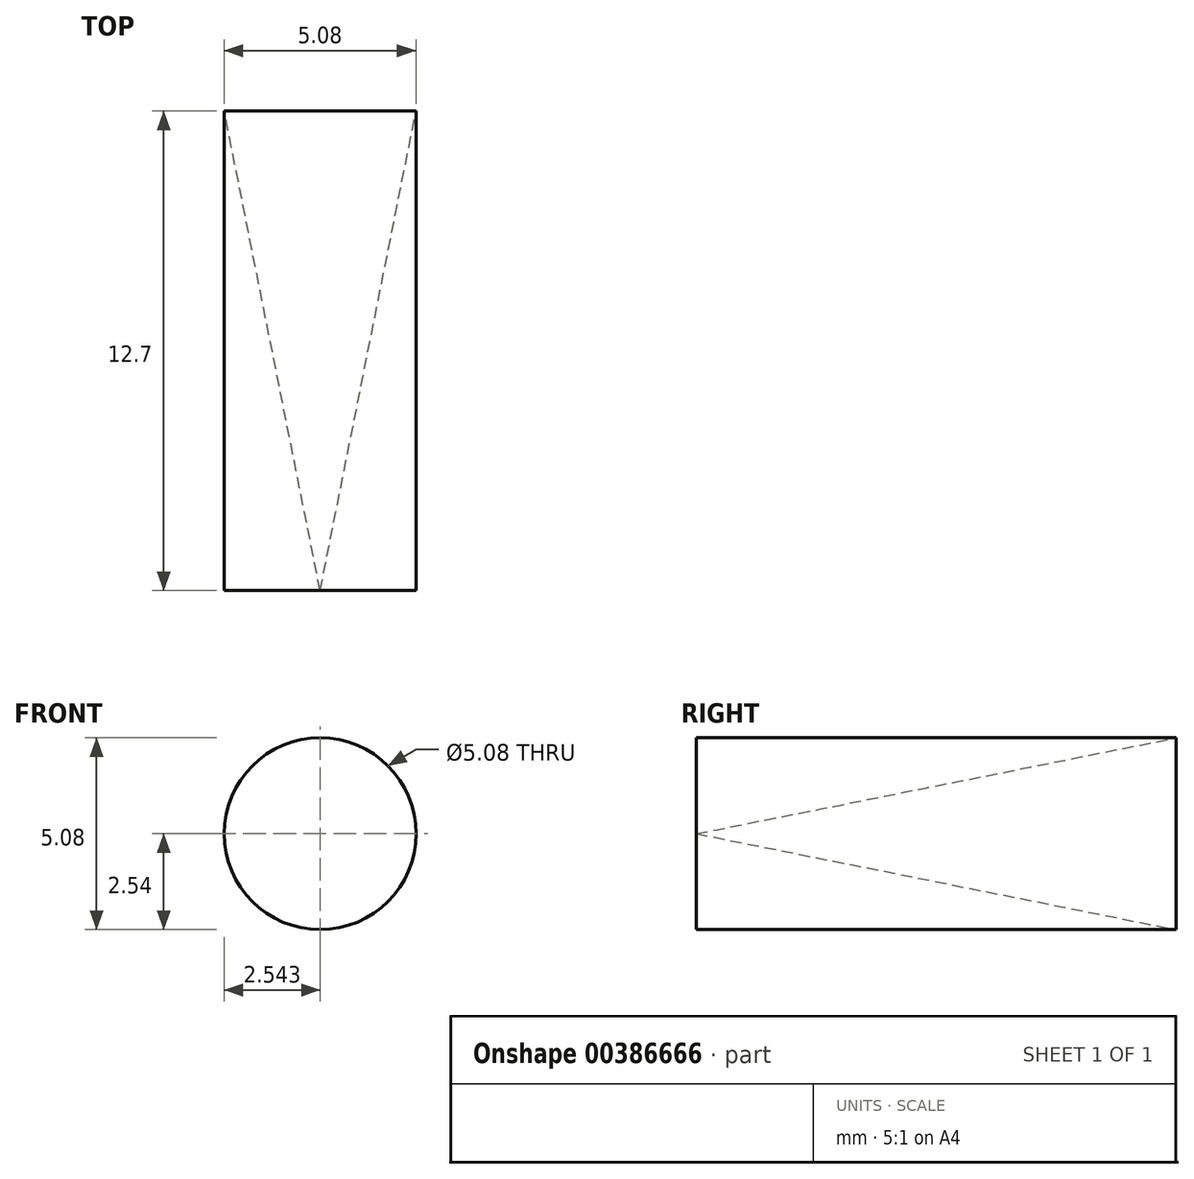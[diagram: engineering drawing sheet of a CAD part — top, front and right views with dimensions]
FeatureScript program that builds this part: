
annotation { "Feature Type Name" : "Feature", "Feature Type Description" : "" }
export const myFeature = defineFeature(function(context is Context, id is Id, definition is map)
    precondition{}
    {
        {
            var Q0;
            Q0=qCreatedBy(makeId("Top.planeOp"),FACE);
            var sketch = newSketch(context, id + "F0", { "sketchPlane" : qUnion([Q0])});
            skLineSegment(sketch, "E0", {"start": v(-59.2, 28.21) * mm, "end": v(-59.2, 15.51) * mm});
            skLineSegment(sketch, "E1", {"start": v(-59.2, 15.51) * mm, "end": v(-56.67, 15.51) * mm});
            skLineSegment(sketch, "E2", {"start": v(-56.67, 15.51) * mm, "end": v(-59.2, 28.21) * mm});
            skLineSegment(sketch, "E3", {"start": v(-56.67, 28.21) * mm, "end": v(-56.67, 15.51) * mm, "construction": true});
            skSolve(sketch);
        }
        {
            var Q0;
            Q0=makeQuery(id+"F0.imprint","IMPRINT",FACE,{"disambiguationData":[TD([[makeQuery(id+"F0.imprint","IMPRINT",EDGE,{"derivedFrom":sQuery(id+"F0.wireOp",EDGE,"E0")}),1.0]])]});
            var Q1;
            Q1=sQuery(id+"F0.wireOp",EDGE,"E2");
            var Q2;
            Q2=sQuery(id+"F0.wireOp",EDGE,"E3");
            revolve(context, id + "F1", {"bodyType" : ToolBodyType.SURFACE, "operationType" : NewBodyOperationType.INTERSECT, "entities" : qUnion([Q0]), "surfaceEntities" : qUnion([Q1]), "axis" : qUnion([Q2]), "revolveType" : RevolveType.FULL, "oppositeDirection" : true});
        }
        {
            var Q0;
            Q0=sQuery(id+"F0.wireOp",EDGE,"E0");
            var Q1;
            Q1=sQuery(id+"F0.wireOp",EDGE,"E3");
            revolve(context, id + "F2", {"bodyType" : ToolBodyType.SURFACE, "surfaceEntities" : qUnion([Q0]), "axis" : qUnion([Q1]), "revolveType" : RevolveType.FULL});
        }
    });
